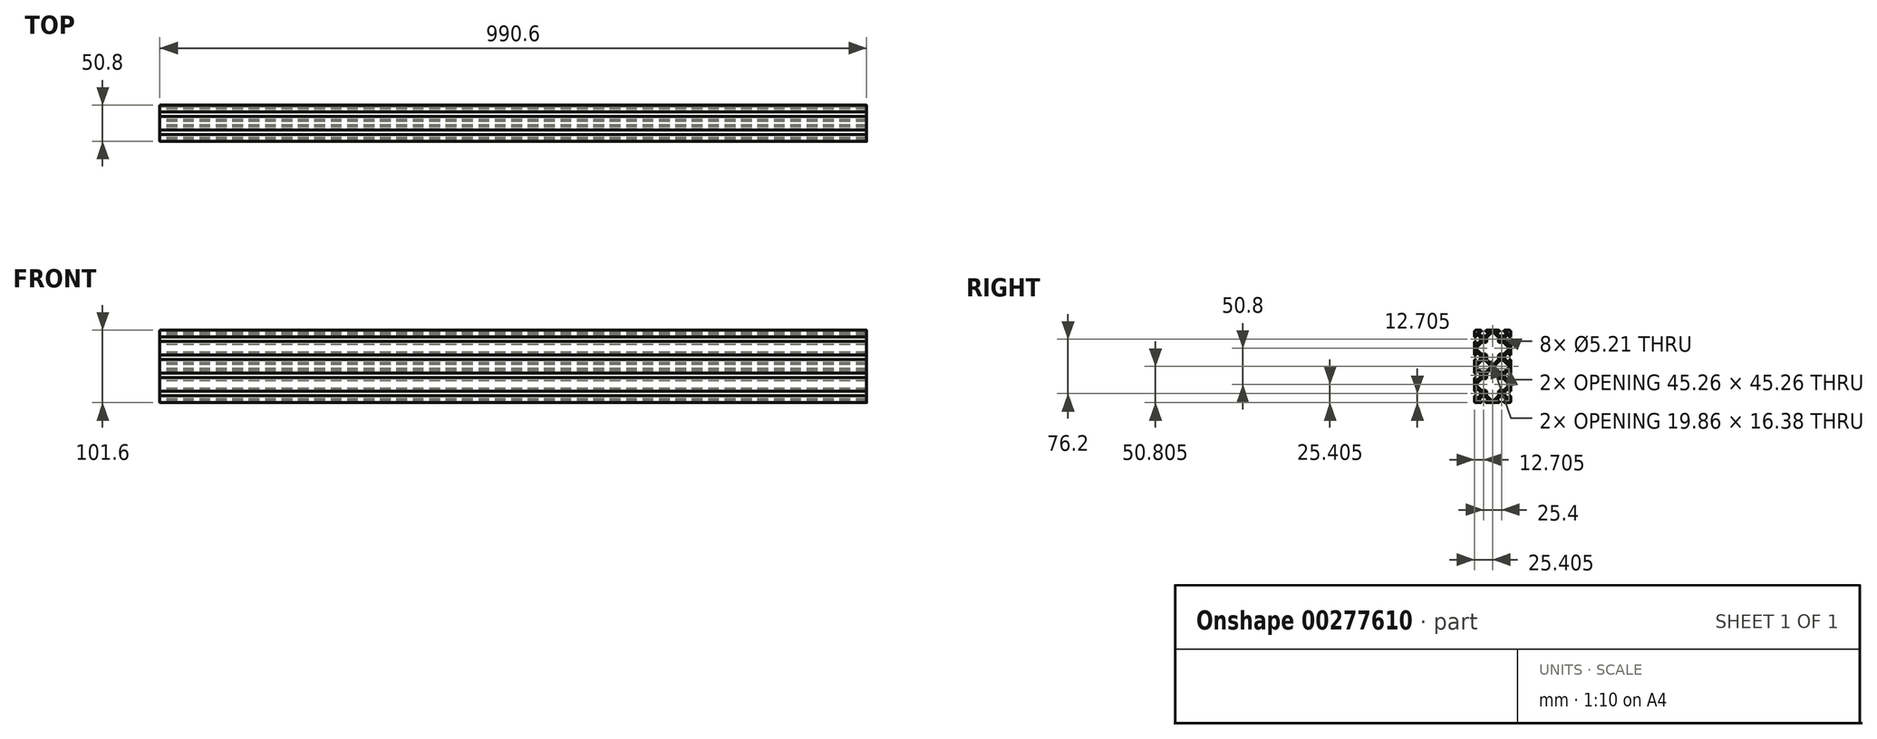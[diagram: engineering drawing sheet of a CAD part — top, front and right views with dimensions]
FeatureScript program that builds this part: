
annotation { "Feature Type Name" : "Feature", "Feature Type Description" : "" }
export const myFeature = defineFeature(function(context is Context, id is Id, definition is map)
    precondition{}
    {
        {
            var Q0;
            Q0=qCreatedBy(makeId("Right.planeOp"),FACE);
            var sketch = newSketch(context, id + "F0", { "sketchPlane" : qUnion([Q0])});
            skArc(sketch, "E0", {"start": v(-121.68, 46.24) * mm, "mid": v(-122.9, 46) * mm, "end": v(-123.92, 45.3) * mm});
            skLineSegment(sketch, "E1", {"start": v(-123.92, 45.3) * mm, "end": v(-129.12, 40.11) * mm});
            skArc(sketch, "E2", {"start": v(-129.12, 40.11) * mm, "mid": v(-129.97, 38.04) * mm, "end": v(-129.12, 35.98) * mm});
            skLineSegment(sketch, "E3", {"start": v(-129.12, 35.98) * mm, "end": v(-123.92, 30.78) * mm});
            skArc(sketch, "E4", {"start": v(-123.92, 30.78) * mm, "mid": v(-122.9, 30.1) * mm, "end": v(-121.68, 29.85) * mm});
            skLineSegment(sketch, "E5", {"start": v(-121.68, 29.85) * mm, "end": v(-118.41, 29.85) * mm});
            skArc(sketch, "E6", {"start": v(-118.41, 29.85) * mm, "mid": v(-117.2, 30.1) * mm, "end": v(-116.17, 30.78) * mm});
            skLineSegment(sketch, "E7", {"start": v(-116.17, 30.78) * mm, "end": v(-110.97, 35.98) * mm});
            skArc(sketch, "E8", {"start": v(-110.97, 35.98) * mm, "mid": v(-110.12, 38.04) * mm, "end": v(-110.97, 40.11) * mm});
            skLineSegment(sketch, "E9", {"start": v(-110.97, 40.11) * mm, "end": v(-116.17, 45.3) * mm});
            skArc(sketch, "E10", {"start": v(-116.17, 45.3) * mm, "mid": v(-117.2, 46) * mm, "end": v(-118.41, 46.24) * mm});
            skArc(sketch, "E11", {"start": v(-121.68, 71.64) * mm, "mid": v(-122.9, 71.4) * mm, "end": v(-123.92, 70.7) * mm});
            skLineSegment(sketch, "E12", {"start": v(-123.92, 70.7) * mm, "end": v(-129.12, 65.51) * mm});
            skArc(sketch, "E13", {"start": v(-129.12, 65.51) * mm, "mid": v(-129.97, 63.44) * mm, "end": v(-129.12, 61.38) * mm});
            skLineSegment(sketch, "E14", {"start": v(-129.12, 61.38) * mm, "end": v(-123.92, 56.18) * mm});
            skArc(sketch, "E15", {"start": v(-123.92, 56.18) * mm, "mid": v(-122.9, 55.5) * mm, "end": v(-121.68, 55.25) * mm});
            skLineSegment(sketch, "E16", {"start": v(-121.68, 55.25) * mm, "end": v(-117.75, 55.25) * mm});
            skArc(sketch, "E17", {"start": v(-115.54, 53.04) * mm, "mid": v(-116.18, 54.6) * mm, "end": v(-117.75, 55.25) * mm});
            skLineSegment(sketch, "E18", {"start": v(-115.54, 53.04) * mm, "end": v(-115.54, 48.71) * mm});
            skArc(sketch, "E19", {"start": v(-115.54, 48.71) * mm, "mid": v(-115.37, 47.87) * mm, "end": v(-114.89, 47.15) * mm});
            skLineSegment(sketch, "E20", {"start": v(-114.89, 47.15) * mm, "end": v(-109.41, 41.67) * mm});
            skArc(sketch, "E21", {"start": v(-109.41, 41.67) * mm, "mid": v(-107.35, 40.82) * mm, "end": v(-105.28, 41.67) * mm});
            skLineSegment(sketch, "E22", {"start": v(-105.28, 41.67) * mm, "end": v(-99.8, 47.15) * mm});
            skArc(sketch, "E23", {"start": v(-99.8, 47.15) * mm, "mid": v(-99.32, 47.87) * mm, "end": v(-99.15, 48.71) * mm});
            skLineSegment(sketch, "E24", {"start": v(-99.15, 48.71) * mm, "end": v(-99.15, 53.04) * mm});
            skArc(sketch, "E25", {"start": v(-96.94, 55.25) * mm, "mid": v(-98.5, 54.6) * mm, "end": v(-99.15, 53.04) * mm});
            skLineSegment(sketch, "E26", {"start": v(-96.94, 55.25) * mm, "end": v(-93.01, 55.25) * mm});
            skArc(sketch, "E27", {"start": v(-93.01, 55.25) * mm, "mid": v(-91.8, 55.5) * mm, "end": v(-90.77, 56.18) * mm});
            skLineSegment(sketch, "E28", {"start": v(-90.77, 56.18) * mm, "end": v(-85.57, 61.38) * mm});
            skArc(sketch, "E29", {"start": v(-85.57, 61.38) * mm, "mid": v(-84.72, 63.44) * mm, "end": v(-85.57, 65.51) * mm});
            skLineSegment(sketch, "E30", {"start": v(-85.57, 65.51) * mm, "end": v(-90.77, 70.7) * mm});
            skArc(sketch, "E31", {"start": v(-90.77, 70.7) * mm, "mid": v(-91.8, 71.4) * mm, "end": v(-93.01, 71.64) * mm});
            skLineSegment(sketch, "E32", {"start": v(-93.01, 71.64) * mm, "end": v(-96.94, 71.64) * mm});
            skArc(sketch, "E33", {"start": v(-99.15, 73.85) * mm, "mid": v(-98.5, 72.28) * mm, "end": v(-96.94, 71.64) * mm});
            skLineSegment(sketch, "E34", {"start": v(-99.15, 73.85) * mm, "end": v(-99.15, 78.18) * mm});
            skArc(sketch, "E35", {"start": v(-99.15, 78.18) * mm, "mid": v(-99.32, 79.02) * mm, "end": v(-99.8, 79.74) * mm});
            skLineSegment(sketch, "E36", {"start": v(-99.8, 79.74) * mm, "end": v(-105.28, 85.22) * mm});
            skArc(sketch, "E37", {"start": v(-105.28, 85.22) * mm, "mid": v(-107.35, 86.07) * mm, "end": v(-109.41, 85.22) * mm});
            skLineSegment(sketch, "E38", {"start": v(-109.41, 85.22) * mm, "end": v(-114.89, 79.74) * mm});
            skArc(sketch, "E39", {"start": v(-114.89, 79.74) * mm, "mid": v(-115.37, 79.02) * mm, "end": v(-115.54, 78.18) * mm});
            skLineSegment(sketch, "E40", {"start": v(-115.54, 78.18) * mm, "end": v(-115.54, 73.85) * mm});
            skArc(sketch, "E41", {"start": v(-117.75, 71.64) * mm, "mid": v(-116.18, 72.28) * mm, "end": v(-115.54, 73.85) * mm});
            skArc(sketch, "E42", {"start": v(-121.68, 20.84) * mm, "mid": v(-122.9, 20.6) * mm, "end": v(-123.92, 19.9) * mm});
            skLineSegment(sketch, "E43", {"start": v(-123.92, 19.9) * mm, "end": v(-129.12, 14.71) * mm});
            skArc(sketch, "E44", {"start": v(-129.12, 14.71) * mm, "mid": v(-129.97, 12.64) * mm, "end": v(-129.12, 10.58) * mm});
            skLineSegment(sketch, "E45", {"start": v(-129.12, 10.58) * mm, "end": v(-123.92, 5.38) * mm});
            skArc(sketch, "E46", {"start": v(-123.92, 5.38) * mm, "mid": v(-122.9, 4.7) * mm, "end": v(-121.68, 4.45) * mm});
            skLineSegment(sketch, "E47", {"start": v(-121.68, 4.45) * mm, "end": v(-117.75, 4.45) * mm});
            skArc(sketch, "E48", {"start": v(-115.54, 2.24) * mm, "mid": v(-116.18, 3.8) * mm, "end": v(-117.75, 4.45) * mm});
            skLineSegment(sketch, "E49", {"start": v(-115.54, 2.24) * mm, "end": v(-115.54, -2.09) * mm});
            skArc(sketch, "E50", {"start": v(-115.54, -2.09) * mm, "mid": v(-115.37, -2.93) * mm, "end": v(-114.89, -3.65) * mm});
            skLineSegment(sketch, "E51", {"start": v(-114.89, -3.65) * mm, "end": v(-109.41, -9.13) * mm});
            skArc(sketch, "E52", {"start": v(-109.41, -9.13) * mm, "mid": v(-107.35, -9.98) * mm, "end": v(-105.28, -9.13) * mm});
            skLineSegment(sketch, "E53", {"start": v(-105.28, -9.13) * mm, "end": v(-99.8, -3.65) * mm});
            skArc(sketch, "E54", {"start": v(-99.8, -3.65) * mm, "mid": v(-99.32, -2.93) * mm, "end": v(-99.15, -2.09) * mm});
            skLineSegment(sketch, "E55", {"start": v(-99.15, -2.09) * mm, "end": v(-99.15, 2.24) * mm});
            skArc(sketch, "E56", {"start": v(-96.94, 4.45) * mm, "mid": v(-98.5, 3.8) * mm, "end": v(-99.15, 2.24) * mm});
            skLineSegment(sketch, "E57", {"start": v(-96.94, 4.45) * mm, "end": v(-93.01, 4.45) * mm});
            skArc(sketch, "E58", {"start": v(-93.01, 4.45) * mm, "mid": v(-91.8, 4.7) * mm, "end": v(-90.77, 5.38) * mm});
            skLineSegment(sketch, "E59", {"start": v(-90.77, 5.38) * mm, "end": v(-85.57, 10.58) * mm});
            skArc(sketch, "E60", {"start": v(-85.57, 10.58) * mm, "mid": v(-84.72, 12.64) * mm, "end": v(-85.57, 14.71) * mm});
            skLineSegment(sketch, "E61", {"start": v(-85.57, 14.71) * mm, "end": v(-90.77, 19.9) * mm});
            skArc(sketch, "E62", {"start": v(-90.77, 19.9) * mm, "mid": v(-91.8, 20.6) * mm, "end": v(-93.01, 20.84) * mm});
            skLineSegment(sketch, "E63", {"start": v(-93.01, 20.84) * mm, "end": v(-96.94, 20.84) * mm});
            skArc(sketch, "E64", {"start": v(-99.15, 23.05) * mm, "mid": v(-98.5, 21.48) * mm, "end": v(-96.94, 20.84) * mm});
            skLineSegment(sketch, "E65", {"start": v(-99.15, 23.05) * mm, "end": v(-99.15, 27.38) * mm});
            skArc(sketch, "E66", {"start": v(-99.15, 27.38) * mm, "mid": v(-99.32, 28.22) * mm, "end": v(-99.8, 28.94) * mm});
            skLineSegment(sketch, "E67", {"start": v(-99.8, 28.94) * mm, "end": v(-105.28, 34.42) * mm});
            skArc(sketch, "E68", {"start": v(-105.28, 34.42) * mm, "mid": v(-107.35, 35.27) * mm, "end": v(-109.41, 34.42) * mm});
            skLineSegment(sketch, "E69", {"start": v(-109.41, 34.42) * mm, "end": v(-114.89, 28.94) * mm});
            skArc(sketch, "E70", {"start": v(-114.89, 28.94) * mm, "mid": v(-115.37, 28.22) * mm, "end": v(-115.54, 27.38) * mm});
            skLineSegment(sketch, "E71", {"start": v(-115.54, 27.38) * mm, "end": v(-115.54, 23.05) * mm});
            skArc(sketch, "E72", {"start": v(-117.75, 20.84) * mm, "mid": v(-116.18, 21.48) * mm, "end": v(-115.54, 23.05) * mm});
            skArc(sketch, "E73", {"start": v(-96.28, 46.24) * mm, "mid": v(-97.5, 46) * mm, "end": v(-98.52, 45.3) * mm});
            skLineSegment(sketch, "E74", {"start": v(-98.52, 45.3) * mm, "end": v(-103.72, 40.11) * mm});
            skArc(sketch, "E75", {"start": v(-103.72, 40.11) * mm, "mid": v(-104.57, 38.04) * mm, "end": v(-103.72, 35.98) * mm});
            skLineSegment(sketch, "E76", {"start": v(-103.72, 35.98) * mm, "end": v(-98.52, 30.78) * mm});
            skArc(sketch, "E77", {"start": v(-98.52, 30.78) * mm, "mid": v(-97.5, 30.1) * mm, "end": v(-96.28, 29.85) * mm});
            skLineSegment(sketch, "E78", {"start": v(-96.28, 29.85) * mm, "end": v(-93.01, 29.85) * mm});
            skArc(sketch, "E79", {"start": v(-93.01, 29.85) * mm, "mid": v(-91.8, 30.1) * mm, "end": v(-90.77, 30.78) * mm});
            skLineSegment(sketch, "E80", {"start": v(-90.77, 30.78) * mm, "end": v(-85.57, 35.98) * mm});
            skArc(sketch, "E81", {"start": v(-85.57, 35.98) * mm, "mid": v(-84.72, 38.04) * mm, "end": v(-85.57, 40.11) * mm});
            skLineSegment(sketch, "E82", {"start": v(-85.57, 40.11) * mm, "end": v(-90.77, 45.3) * mm});
            skArc(sketch, "E83", {"start": v(-90.77, 45.3) * mm, "mid": v(-91.8, 46) * mm, "end": v(-93.01, 46.24) * mm});
            skArc(sketch, "E84", {"start": v(-130.54, 46.44) * mm, "mid": v(-131.64, 47.55) * mm, "end": v(-132.75, 46.44) * mm});
            skLineSegment(sketch, "E85", {"start": v(-130.54, 44.27) * mm, "end": v(-130.54, 46.44) * mm});
            skArc(sketch, "E86", {"start": v(-130.54, 44.27) * mm, "mid": v(-129.9, 43.33) * mm, "end": v(-128.8, 43.55) * mm});
            skLineSegment(sketch, "E87", {"start": v(-125.48, 46.87) * mm, "end": v(-128.8, 43.55) * mm});
            skArc(sketch, "E88", {"start": v(-125.48, 46.87) * mm, "mid": v(-124.8, 47.9) * mm, "end": v(-124.55, 49.11) * mm});
            skLineSegment(sketch, "E89", {"start": v(-124.55, 52.38) * mm, "end": v(-124.55, 49.11) * mm});
            skArc(sketch, "E90", {"start": v(-124.55, 52.38) * mm, "mid": v(-124.8, 53.6) * mm, "end": v(-125.48, 54.62) * mm});
            skLineSegment(sketch, "E91", {"start": v(-128.8, 57.94) * mm, "end": v(-125.48, 54.62) * mm});
            skArc(sketch, "E92", {"start": v(-128.8, 57.94) * mm, "mid": v(-129.9, 58.16) * mm, "end": v(-130.54, 57.22) * mm});
            skLineSegment(sketch, "E93", {"start": v(-130.54, 55.05) * mm, "end": v(-130.54, 57.22) * mm});
            skArc(sketch, "E94", {"start": v(-132.75, 55.05) * mm, "mid": v(-131.64, 53.94) * mm, "end": v(-130.54, 55.05) * mm});
            skArc(sketch, "E95", {"start": v(-130.54, 71.84) * mm, "mid": v(-131.64, 72.95) * mm, "end": v(-132.75, 71.84) * mm});
            skLineSegment(sketch, "E96", {"start": v(-130.54, 69.67) * mm, "end": v(-130.54, 71.84) * mm});
            skArc(sketch, "E97", {"start": v(-130.54, 69.67) * mm, "mid": v(-129.9, 68.73) * mm, "end": v(-128.8, 68.95) * mm});
            skLineSegment(sketch, "E98", {"start": v(-125.48, 72.27) * mm, "end": v(-128.8, 68.95) * mm});
            skArc(sketch, "E99", {"start": v(-125.48, 72.27) * mm, "mid": v(-124.8, 73.3) * mm, "end": v(-124.55, 74.51) * mm});
            skLineSegment(sketch, "E100", {"start": v(-124.55, 77.78) * mm, "end": v(-124.55, 74.51) * mm});
            skArc(sketch, "E101", {"start": v(-124.55, 77.78) * mm, "mid": v(-124.8, 79) * mm, "end": v(-125.48, 80.02) * mm});
            skLineSegment(sketch, "E102", {"start": v(-128.8, 83.34) * mm, "end": v(-125.48, 80.02) * mm});
            skArc(sketch, "E103", {"start": v(-128.8, 83.34) * mm, "mid": v(-129.9, 83.56) * mm, "end": v(-130.54, 82.62) * mm});
            skLineSegment(sketch, "E104", {"start": v(-130.54, 80.45) * mm, "end": v(-130.54, 82.62) * mm});
            skArc(sketch, "E105", {"start": v(-132.75, 80.45) * mm, "mid": v(-131.64, 79.34) * mm, "end": v(-130.54, 80.45) * mm});
            skLineSegment(sketch, "E106", {"start": v(-123.92, 81.58) * mm, "end": v(-127.24, 84.9) * mm});
            skArc(sketch, "E107", {"start": v(-123.92, 81.58) * mm, "mid": v(-122.9, 80.9) * mm, "end": v(-121.68, 80.65) * mm});
            skLineSegment(sketch, "E108", {"start": v(-118.41, 80.65) * mm, "end": v(-121.68, 80.65) * mm});
            skArc(sketch, "E109", {"start": v(-118.41, 80.65) * mm, "mid": v(-117.2, 80.9) * mm, "end": v(-116.17, 81.58) * mm});
            skLineSegment(sketch, "E110", {"start": v(-112.85, 84.9) * mm, "end": v(-116.17, 81.58) * mm});
            skArc(sketch, "E111", {"start": v(-112.85, 84.9) * mm, "mid": v(-112.63, 86) * mm, "end": v(-113.57, 86.63) * mm});
            skLineSegment(sketch, "E112", {"start": v(-115.74, 86.63) * mm, "end": v(-113.57, 86.63) * mm});
            skArc(sketch, "E113", {"start": v(-115.74, 88.84) * mm, "mid": v(-116.85, 87.74) * mm, "end": v(-115.74, 86.63) * mm});
            skLineSegment(sketch, "E114", {"start": v(-98.95, 88.84) * mm, "end": v(-115.74, 88.84) * mm});
            skArc(sketch, "E115", {"start": v(-98.95, 86.63) * mm, "mid": v(-97.84, 87.74) * mm, "end": v(-98.95, 88.84) * mm});
            skLineSegment(sketch, "E116", {"start": v(-101.12, 86.63) * mm, "end": v(-98.95, 86.63) * mm});
            skArc(sketch, "E117", {"start": v(-101.12, 86.63) * mm, "mid": v(-102.06, 86) * mm, "end": v(-101.84, 84.9) * mm});
            skLineSegment(sketch, "E118", {"start": v(-98.52, 81.58) * mm, "end": v(-101.84, 84.9) * mm});
            skArc(sketch, "E119", {"start": v(-98.52, 81.58) * mm, "mid": v(-97.5, 80.9) * mm, "end": v(-96.28, 80.65) * mm});
            skLineSegment(sketch, "E120", {"start": v(-93.01, 80.65) * mm, "end": v(-96.28, 80.65) * mm});
            skArc(sketch, "E121", {"start": v(-93.01, 80.65) * mm, "mid": v(-91.8, 80.9) * mm, "end": v(-90.77, 81.58) * mm});
            skLineSegment(sketch, "E122", {"start": v(-87.45, 84.9) * mm, "end": v(-90.77, 81.58) * mm});
            skArc(sketch, "E123", {"start": v(-87.45, 84.9) * mm, "mid": v(-87.23, 86) * mm, "end": v(-88.17, 86.63) * mm});
            skLineSegment(sketch, "E124", {"start": v(-90.34, 86.63) * mm, "end": v(-88.17, 86.63) * mm});
            skArc(sketch, "E125", {"start": v(-90.34, 88.84) * mm, "mid": v(-91.45, 87.74) * mm, "end": v(-90.34, 86.63) * mm});
            skArc(sketch, "E126", {"start": v(-81.95, 86.72) * mm, "mid": v(-82.56, 88.23) * mm, "end": v(-84.07, 88.84) * mm});
            skArc(sketch, "E127", {"start": v(-84.16, 80.45) * mm, "mid": v(-83.05, 79.34) * mm, "end": v(-81.95, 80.45) * mm});
            skLineSegment(sketch, "E128", {"start": v(-84.16, 82.62) * mm, "end": v(-84.16, 80.45) * mm});
            skArc(sketch, "E129", {"start": v(-84.16, 82.62) * mm, "mid": v(-84.78, 83.56) * mm, "end": v(-85.89, 83.34) * mm});
            skLineSegment(sketch, "E130", {"start": v(-89.2, 80.02) * mm, "end": v(-85.89, 83.34) * mm});
            skArc(sketch, "E131", {"start": v(-89.2, 80.02) * mm, "mid": v(-89.9, 79) * mm, "end": v(-90.14, 77.78) * mm});
            skLineSegment(sketch, "E132", {"start": v(-90.14, 74.51) * mm, "end": v(-90.14, 77.78) * mm});
            skArc(sketch, "E133", {"start": v(-90.14, 74.51) * mm, "mid": v(-89.9, 73.3) * mm, "end": v(-89.2, 72.27) * mm});
            skLineSegment(sketch, "E134", {"start": v(-85.89, 68.95) * mm, "end": v(-89.2, 72.27) * mm});
            skArc(sketch, "E135", {"start": v(-85.89, 68.95) * mm, "mid": v(-84.78, 68.73) * mm, "end": v(-84.16, 69.67) * mm});
            skLineSegment(sketch, "E136", {"start": v(-84.16, 71.84) * mm, "end": v(-84.16, 69.67) * mm});
            skArc(sketch, "E137", {"start": v(-81.95, 71.84) * mm, "mid": v(-83.05, 72.95) * mm, "end": v(-84.16, 71.84) * mm});
            skArc(sketch, "E138", {"start": v(-84.16, 55.05) * mm, "mid": v(-83.05, 53.94) * mm, "end": v(-81.95, 55.05) * mm});
            skLineSegment(sketch, "E139", {"start": v(-84.16, 57.22) * mm, "end": v(-84.16, 55.05) * mm});
            skArc(sketch, "E140", {"start": v(-84.16, 57.22) * mm, "mid": v(-84.78, 58.16) * mm, "end": v(-85.89, 57.94) * mm});
            skLineSegment(sketch, "E141", {"start": v(-89.2, 54.62) * mm, "end": v(-85.89, 57.94) * mm});
            skArc(sketch, "E142", {"start": v(-89.2, 54.62) * mm, "mid": v(-89.9, 53.6) * mm, "end": v(-90.14, 52.38) * mm});
            skLineSegment(sketch, "E143", {"start": v(-90.14, 49.11) * mm, "end": v(-90.14, 52.38) * mm});
            skArc(sketch, "E144", {"start": v(-90.14, 49.11) * mm, "mid": v(-89.9, 47.9) * mm, "end": v(-89.2, 46.87) * mm});
            skLineSegment(sketch, "E145", {"start": v(-85.89, 43.55) * mm, "end": v(-89.2, 46.87) * mm});
            skArc(sketch, "E146", {"start": v(-85.89, 43.55) * mm, "mid": v(-84.78, 43.33) * mm, "end": v(-84.16, 44.27) * mm});
            skLineSegment(sketch, "E147", {"start": v(-84.16, 46.44) * mm, "end": v(-84.16, 44.27) * mm});
            skArc(sketch, "E148", {"start": v(-81.95, 46.44) * mm, "mid": v(-83.05, 47.55) * mm, "end": v(-84.16, 46.44) * mm});
            skArc(sketch, "E149", {"start": v(-84.16, 29.65) * mm, "mid": v(-83.05, 28.54) * mm, "end": v(-81.95, 29.65) * mm});
            skLineSegment(sketch, "E150", {"start": v(-84.16, 31.82) * mm, "end": v(-84.16, 29.65) * mm});
            skArc(sketch, "E151", {"start": v(-84.16, 31.82) * mm, "mid": v(-84.78, 32.76) * mm, "end": v(-85.89, 32.54) * mm});
            skLineSegment(sketch, "E152", {"start": v(-89.2, 29.22) * mm, "end": v(-85.89, 32.54) * mm});
            skArc(sketch, "E153", {"start": v(-89.2, 29.22) * mm, "mid": v(-89.9, 28.2) * mm, "end": v(-90.14, 26.98) * mm});
            skLineSegment(sketch, "E154", {"start": v(-90.14, 23.71) * mm, "end": v(-90.14, 26.98) * mm});
            skArc(sketch, "E155", {"start": v(-90.14, 23.71) * mm, "mid": v(-89.9, 22.5) * mm, "end": v(-89.2, 21.47) * mm});
            skLineSegment(sketch, "E156", {"start": v(-85.89, 18.15) * mm, "end": v(-89.2, 21.47) * mm});
            skArc(sketch, "E157", {"start": v(-85.89, 18.15) * mm, "mid": v(-84.78, 17.93) * mm, "end": v(-84.16, 18.87) * mm});
            skLineSegment(sketch, "E158", {"start": v(-84.16, 21.04) * mm, "end": v(-84.16, 18.87) * mm});
            skArc(sketch, "E159", {"start": v(-81.95, 21.04) * mm, "mid": v(-83.05, 22.15) * mm, "end": v(-84.16, 21.04) * mm});
            skArc(sketch, "E160", {"start": v(-84.16, 4.25) * mm, "mid": v(-83.05, 3.14) * mm, "end": v(-81.95, 4.25) * mm});
            skLineSegment(sketch, "E161", {"start": v(-84.16, 6.42) * mm, "end": v(-84.16, 4.25) * mm});
            skArc(sketch, "E162", {"start": v(-84.16, 6.42) * mm, "mid": v(-84.78, 7.36) * mm, "end": v(-85.89, 7.14) * mm});
            skLineSegment(sketch, "E163", {"start": v(-89.2, 3.82) * mm, "end": v(-85.89, 7.14) * mm});
            skArc(sketch, "E164", {"start": v(-89.2, 3.82) * mm, "mid": v(-89.9, 2.8) * mm, "end": v(-90.14, 1.58) * mm});
            skLineSegment(sketch, "E165", {"start": v(-90.14, -1.69) * mm, "end": v(-90.14, 1.58) * mm});
            skArc(sketch, "E166", {"start": v(-90.14, -1.69) * mm, "mid": v(-89.9, -2.9) * mm, "end": v(-89.2, -3.93) * mm});
            skLineSegment(sketch, "E167", {"start": v(-85.89, -7.25) * mm, "end": v(-89.2, -3.93) * mm});
            skArc(sketch, "E168", {"start": v(-85.89, -7.25) * mm, "mid": v(-84.78, -7.47) * mm, "end": v(-84.16, -6.53) * mm});
            skLineSegment(sketch, "E169", {"start": v(-84.16, -4.36) * mm, "end": v(-84.16, -6.53) * mm});
            skArc(sketch, "E170", {"start": v(-81.95, -4.36) * mm, "mid": v(-83.05, -3.25) * mm, "end": v(-84.16, -4.36) * mm});
            skArc(sketch, "E171", {"start": v(-84.07, -12.76) * mm, "mid": v(-82.56, -12.14) * mm, "end": v(-81.95, -10.63) * mm});
            skArc(sketch, "E172", {"start": v(-90.34, -10.55) * mm, "mid": v(-91.45, -11.65) * mm, "end": v(-90.34, -12.76) * mm});
            skLineSegment(sketch, "E173", {"start": v(-88.17, -10.55) * mm, "end": v(-90.34, -10.55) * mm});
            skArc(sketch, "E174", {"start": v(-88.17, -10.55) * mm, "mid": v(-87.23, -9.92) * mm, "end": v(-87.45, -8.81) * mm});
            skLineSegment(sketch, "E175", {"start": v(-90.77, -5.5) * mm, "end": v(-87.45, -8.81) * mm});
            skArc(sketch, "E176", {"start": v(-90.77, -5.5) * mm, "mid": v(-91.8, -4.8) * mm, "end": v(-93.01, -4.56) * mm});
            skLineSegment(sketch, "E177", {"start": v(-96.28, -4.56) * mm, "end": v(-93.01, -4.56) * mm});
            skArc(sketch, "E178", {"start": v(-96.28, -4.56) * mm, "mid": v(-97.5, -4.8) * mm, "end": v(-98.52, -5.5) * mm});
            skLineSegment(sketch, "E179", {"start": v(-101.84, -8.81) * mm, "end": v(-98.52, -5.5) * mm});
            skArc(sketch, "E180", {"start": v(-101.84, -8.81) * mm, "mid": v(-102.06, -9.92) * mm, "end": v(-101.12, -10.55) * mm});
            skLineSegment(sketch, "E181", {"start": v(-98.95, -10.55) * mm, "end": v(-101.12, -10.55) * mm});
            skArc(sketch, "E182", {"start": v(-98.95, -12.76) * mm, "mid": v(-97.84, -11.65) * mm, "end": v(-98.95, -10.55) * mm});
            skArc(sketch, "E183", {"start": v(-115.74, -10.55) * mm, "mid": v(-116.85, -11.65) * mm, "end": v(-115.74, -12.76) * mm});
            skLineSegment(sketch, "E184", {"start": v(-113.57, -10.55) * mm, "end": v(-115.74, -10.55) * mm});
            skArc(sketch, "E185", {"start": v(-113.57, -10.55) * mm, "mid": v(-112.63, -9.92) * mm, "end": v(-112.85, -8.81) * mm});
            skLineSegment(sketch, "E186", {"start": v(-116.17, -5.5) * mm, "end": v(-112.85, -8.81) * mm});
            skArc(sketch, "E187", {"start": v(-116.17, -5.5) * mm, "mid": v(-117.2, -4.8) * mm, "end": v(-118.41, -4.56) * mm});
            skLineSegment(sketch, "E188", {"start": v(-121.68, -4.56) * mm, "end": v(-118.41, -4.56) * mm});
            skArc(sketch, "E189", {"start": v(-121.68, -4.56) * mm, "mid": v(-122.9, -4.8) * mm, "end": v(-123.92, -5.5) * mm});
            skLineSegment(sketch, "E190", {"start": v(-127.24, -8.81) * mm, "end": v(-123.92, -5.5) * mm});
            skArc(sketch, "E191", {"start": v(-127.24, -8.81) * mm, "mid": v(-127.46, -9.92) * mm, "end": v(-126.52, -10.55) * mm});
            skLineSegment(sketch, "E192", {"start": v(-124.35, -10.55) * mm, "end": v(-126.52, -10.55) * mm});
            skArc(sketch, "E193", {"start": v(-124.35, -12.76) * mm, "mid": v(-123.24, -11.65) * mm, "end": v(-124.35, -10.55) * mm});
            skArc(sketch, "E194", {"start": v(-132.75, -10.63) * mm, "mid": v(-132.13, -12.14) * mm, "end": v(-130.62, -12.76) * mm});
            skArc(sketch, "E195", {"start": v(-130.54, -4.36) * mm, "mid": v(-131.64, -3.25) * mm, "end": v(-132.75, -4.36) * mm});
            skLineSegment(sketch, "E196", {"start": v(-130.54, -6.53) * mm, "end": v(-130.54, -4.36) * mm});
            skArc(sketch, "E197", {"start": v(-130.54, -6.53) * mm, "mid": v(-129.9, -7.47) * mm, "end": v(-128.8, -7.25) * mm});
            skLineSegment(sketch, "E198", {"start": v(-125.48, -3.93) * mm, "end": v(-128.8, -7.25) * mm});
            skArc(sketch, "E199", {"start": v(-125.48, -3.93) * mm, "mid": v(-124.8, -2.9) * mm, "end": v(-124.55, -1.69) * mm});
            skLineSegment(sketch, "E200", {"start": v(-124.55, 1.58) * mm, "end": v(-124.55, -1.69) * mm});
            skArc(sketch, "E201", {"start": v(-124.55, 1.58) * mm, "mid": v(-124.8, 2.8) * mm, "end": v(-125.48, 3.82) * mm});
            skLineSegment(sketch, "E202", {"start": v(-128.8, 7.14) * mm, "end": v(-125.48, 3.82) * mm});
            skArc(sketch, "E203", {"start": v(-128.8, 7.14) * mm, "mid": v(-129.9, 7.36) * mm, "end": v(-130.54, 6.42) * mm});
            skLineSegment(sketch, "E204", {"start": v(-130.54, 4.25) * mm, "end": v(-130.54, 6.42) * mm});
            skArc(sketch, "E205", {"start": v(-132.75, 4.25) * mm, "mid": v(-131.64, 3.14) * mm, "end": v(-130.54, 4.25) * mm});
            skArc(sketch, "E206", {"start": v(-130.54, 21.04) * mm, "mid": v(-131.64, 22.15) * mm, "end": v(-132.75, 21.04) * mm});
            skLineSegment(sketch, "E207", {"start": v(-130.54, 18.87) * mm, "end": v(-130.54, 21.04) * mm});
            skArc(sketch, "E208", {"start": v(-130.54, 18.87) * mm, "mid": v(-129.9, 17.93) * mm, "end": v(-128.8, 18.15) * mm});
            skLineSegment(sketch, "E209", {"start": v(-125.48, 21.47) * mm, "end": v(-128.8, 18.15) * mm});
            skArc(sketch, "E210", {"start": v(-125.48, 21.47) * mm, "mid": v(-124.8, 22.5) * mm, "end": v(-124.55, 23.71) * mm});
            skLineSegment(sketch, "E211", {"start": v(-124.55, 26.98) * mm, "end": v(-124.55, 23.71) * mm});
            skArc(sketch, "E212", {"start": v(-124.55, 26.98) * mm, "mid": v(-124.8, 28.2) * mm, "end": v(-125.48, 29.22) * mm});
            skLineSegment(sketch, "E213", {"start": v(-128.8, 32.54) * mm, "end": v(-125.48, 29.22) * mm});
            skArc(sketch, "E214", {"start": v(-128.8, 32.54) * mm, "mid": v(-129.9, 32.76) * mm, "end": v(-130.54, 31.82) * mm});
            skLineSegment(sketch, "E215", {"start": v(-130.54, 29.65) * mm, "end": v(-130.54, 31.82) * mm});
            skArc(sketch, "E216", {"start": v(-132.75, 29.65) * mm, "mid": v(-131.64, 28.54) * mm, "end": v(-130.54, 29.65) * mm});
            skLineSegment(sketch, "E217", {"start": v(-117.75, 71.64) * mm, "end": v(-121.68, 71.64) * mm});
            skLineSegment(sketch, "E218", {"start": v(-117.75, 20.84) * mm, "end": v(-121.68, 20.84) * mm});
            skCircle(sketch, "E219", {"center": v(-120.05, 76.14) * mm, "radius": 2.6 * mm});
            skCircle(sketch, "E220", {"center": v(-120.05, 50.74) * mm, "radius": 2.6 * mm});
            skLineSegment(sketch, "E221", {"start": v(-93.01, 46.24) * mm, "end": v(-96.28, 46.24) * mm});
            skCircle(sketch, "E222", {"center": v(-94.65, 50.74) * mm, "radius": 2.6 * mm});
            skCircle(sketch, "E223", {"center": v(-94.65, 25.34) * mm, "radius": 2.6 * mm});
            skCircle(sketch, "E224", {"center": v(-94.65, -0.06) * mm, "radius": 2.6 * mm});
            skCircle(sketch, "E225", {"center": v(-94.65, 76.14) * mm, "radius": 2.6 * mm});
            skCircle(sketch, "E226", {"center": v(-120.05, 25.34) * mm, "radius": 2.6 * mm});
            skCircle(sketch, "E227", {"center": v(-120.05, -0.06) * mm, "radius": 2.6 * mm});
            skLineSegment(sketch, "E228", {"start": v(-118.41, 46.24) * mm, "end": v(-121.68, 46.24) * mm});
            skLineSegment(sketch, "E229", {"start": v(-90.34, 88.84) * mm, "end": v(-84.07, 88.84) * mm});
            skLineSegment(sketch, "E230", {"start": v(-81.95, 86.72) * mm, "end": v(-81.95, 80.45) * mm});
            skLineSegment(sketch, "E231", {"start": v(-81.95, 71.84) * mm, "end": v(-81.95, 55.05) * mm});
            skLineSegment(sketch, "E232", {"start": v(-81.95, 29.65) * mm, "end": v(-81.95, 46.44) * mm});
            skLineSegment(sketch, "E233", {"start": v(-81.95, 4.25) * mm, "end": v(-81.95, 21.04) * mm});
            skLineSegment(sketch, "E234", {"start": v(-81.95, -4.36) * mm, "end": v(-81.95, -10.63) * mm});
            skLineSegment(sketch, "E235", {"start": v(-84.07, -12.76) * mm, "end": v(-90.34, -12.76) * mm});
            skLineSegment(sketch, "E236", {"start": v(-98.95, -12.76) * mm, "end": v(-115.74, -12.76) * mm});
            skLineSegment(sketch, "E237", {"start": v(-124.35, -12.76) * mm, "end": v(-130.62, -12.76) * mm});
            skLineSegment(sketch, "E238", {"start": v(-132.75, -4.36) * mm, "end": v(-132.75, -10.63) * mm});
            skLineSegment(sketch, "E239", {"start": v(-132.75, 21.04) * mm, "end": v(-132.75, 4.25) * mm});
            skLineSegment(sketch, "E240", {"start": v(-132.75, 46.44) * mm, "end": v(-132.75, 29.65) * mm});
            skLineSegment(sketch, "E241", {"start": v(-132.75, 71.84) * mm, "end": v(-132.75, 55.05) * mm});
            skArc(sketch, "E242.MirrorCS", {"start": v(-124.35, 88.84) * mm, "mid": v(-123.24, 87.74) * mm, "end": v(-124.35, 86.63) * mm});
            skLineSegment(sketch, "E243.MirrorCS", {"start": v(-124.35, 88.84) * mm, "end": v(-130.62, 88.84) * mm});
            skArc(sketch, "E244.MirrorCS", {"start": v(-132.75, 86.72) * mm, "mid": v(-132.13, 88.23) * mm, "end": v(-130.62, 88.84) * mm});
            skLineSegment(sketch, "E245.MirrorCS", {"start": v(-124.35, 86.63) * mm, "end": v(-126.52, 86.63) * mm});
            skArc(sketch, "E246.MirrorCS", {"start": v(-127.24, 84.9) * mm, "mid": v(-127.46, 86) * mm, "end": v(-126.52, 86.63) * mm});
            skLineSegment(sketch, "E247.MirrorCS", {"start": v(-132.75, 86.72) * mm, "end": v(-132.75, 80.45) * mm});
            skLineSegment(sketch, "E248", {"start": v(-107.35, 40.82) * mm, "end": v(-107.35, 35.27) * mm});
            skPoint(sketch, "E249", {"position": v(-107.35, 38.04) * mm});
            skSolve(sketch);
        }
        {
            var Q0;
            Q0=makeQuery(id+"F0.imprint","IMPRINT",FACE,{"disambiguationData":[TD([[makeQuery(id+"F0.imprint","IMPRINT",EDGE,{"derivedFrom":sQuery(id+"F0.wireOp",EDGE,"E0")}),-1.0]])]});
            extrude(context, id + "F1", {"entities" : qUnion([Q0]), "endBound" : BoundingType.SYMMETRIC, "depth" : 990.6 * mm});
        }
    });
